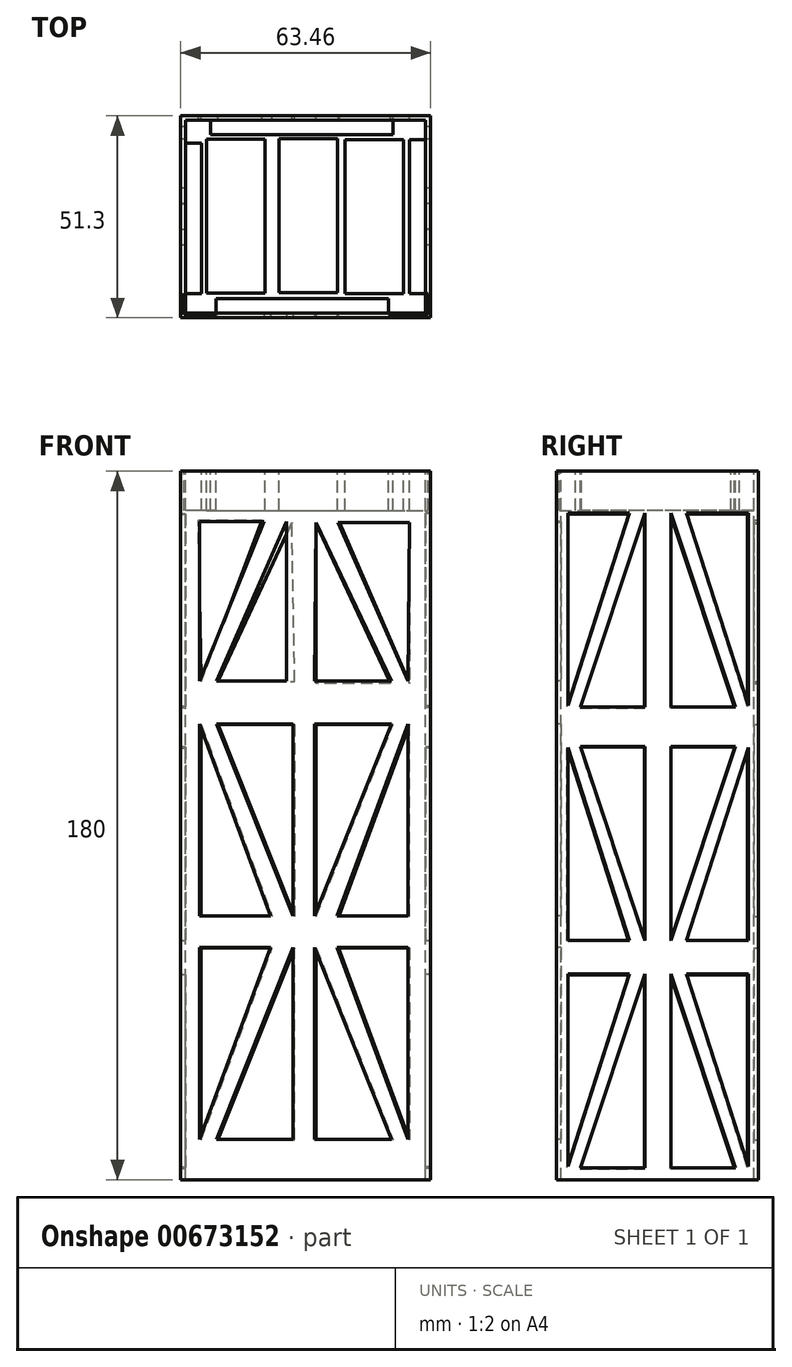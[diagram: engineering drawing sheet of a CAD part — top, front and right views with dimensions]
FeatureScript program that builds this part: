
annotation { "Feature Type Name" : "Feature", "Feature Type Description" : "" }
export const myFeature = defineFeature(function(context is Context, id is Id, definition is map)
    precondition{}
    {
        {
            var Q0;
            Q0=qCreatedBy(makeId("Top.planeOp"),FACE);
            var sketch = newSketch(context, id + "F0", { "sketchPlane" : qUnion([Q0])});
            skLineSegment(sketch, "E0.bottom", {"start": v(-30.5, 24.5) * mm, "end": v(30.5, 24.5) * mm});
            skLineSegment(sketch, "E0.top", {"start": v(-30.5, -24.5) * mm, "end": v(30.5, -24.5) * mm});
            skLineSegment(sketch, "E0.left", {"start": v(-30.5, 24.5) * mm, "end": v(-30.5, -24.5) * mm});
            skLineSegment(sketch, "E0.right", {"start": v(30.5, 24.5) * mm, "end": v(30.5, -24.5) * mm});
            skPoint(sketch, "E0.middle", {"position": v(0, 0) * mm});
            skLineSegment(sketch, "E1.bottom", {"start": v(-31.73, 25.65) * mm, "end": v(31.73, 25.65) * mm});
            skLineSegment(sketch, "E1.top", {"start": v(-31.73, -25.65) * mm, "end": v(31.73, -25.65) * mm});
            skLineSegment(sketch, "E1.left", {"start": v(-31.73, 25.65) * mm, "end": v(-31.73, -25.65) * mm});
            skLineSegment(sketch, "E1.right", {"start": v(31.73, 25.65) * mm, "end": v(31.73, -25.65) * mm});
            skSolve(sketch);
        }
        {
            var Q0;
            Q0=qSketchRegion(id+"F0",true);
            var Q1;
            Q1=qSketchRegion(id+"F2",true);
            extrude(context, id + "F1", {"entities" : qUnion([Q0, Q1]), "oppositeDirection" : true, "depth" : 180 * mm, "offsetDistance" : 25 * mm});
        }
        {
            var Q0;
            Q0=qCreatedBy(makeId("Front.planeOp"),FACE);
            var sketch = newSketch(context, id + "F2", { "sketchPlane" : qUnion([Q0])});
            skLineSegment(sketch, "E2", {"start": v(-37.52, 0) * mm, "end": v(-37.52, -20) * mm});
            skLineSegment(sketch, "E3", {"start": v(38.63, 0) * mm, "end": v(38.63, -20) * mm});
            skSolve(sketch);
        }
        {
            var Q0;
            Q0=qCreatedBy(makeId("Top.planeOp"),FACE);
            var sketch = newSketch(context, id + "F3", { "sketchPlane" : qUnion([Q0])});
            skLineSegment(sketch, "E4.bottom", {"start": v(-26.37, 20.82) * mm, "end": v(26.37, 20.82) * mm});
            skLineSegment(sketch, "E4.top", {"start": v(-26.37, -20.82) * mm, "end": v(26.37, -20.82) * mm});
            skLineSegment(sketch, "E4.left", {"start": v(-26.37, 20.82) * mm, "end": v(-26.37, -20.82) * mm});
            skLineSegment(sketch, "E4.right", {"start": v(26.37, 20.82) * mm, "end": v(26.37, -20.82) * mm});
            skPoint(sketch, "E4.middle", {"position": v(0, 0) * mm});
            skLineSegment(sketch, "E5.bottom", {"start": v(-25.17, 19.7) * mm, "end": v(-10.28, 19.7) * mm});
            skLineSegment(sketch, "E5.top", {"start": v(-25.17, -19.42) * mm, "end": v(-10.28, -19.42) * mm});
            skLineSegment(sketch, "E5.left", {"start": v(-25.17, 19.7) * mm, "end": v(-25.17, -19.42) * mm});
            skLineSegment(sketch, "E5.right", {"start": v(-10.28, 19.7) * mm, "end": v(-10.28, -19.42) * mm});
            skLineSegment(sketch, "E6.bottom", {"start": v(-6.78, 19.79) * mm, "end": v(8.12, 19.79) * mm});
            skLineSegment(sketch, "E6.top", {"start": v(-6.78, -19.34) * mm, "end": v(8.12, -19.34) * mm});
            skLineSegment(sketch, "E6.left", {"start": v(-6.78, 19.79) * mm, "end": v(-6.78, -19.34) * mm});
            skLineSegment(sketch, "E6.right", {"start": v(8.12, 19.79) * mm, "end": v(8.12, -19.34) * mm});
            skLineSegment(sketch, "E7.bottom", {"start": v(10.02, 19.6) * mm, "end": v(24.92, 19.6) * mm});
            skLineSegment(sketch, "E7.top", {"start": v(10.02, -19.52) * mm, "end": v(24.92, -19.52) * mm});
            skLineSegment(sketch, "E7.left", {"start": v(10.02, 19.6) * mm, "end": v(10.02, -19.52) * mm});
            skLineSegment(sketch, "E7.right", {"start": v(24.92, 19.6) * mm, "end": v(24.92, -19.52) * mm});
            skLineSegment(sketch, "E8.bottom", {"start": v(-26.37, 18.7) * mm, "end": v(-30.55, 18.7) * mm});
            skLineSegment(sketch, "E8.top", {"start": v(-26.37, 24.55) * mm, "end": v(-30.55, 24.55) * mm});
            skLineSegment(sketch, "E8.left", {"start": v(-26.37, 18.7) * mm, "end": v(-26.37, 24.55) * mm});
            skLineSegment(sketch, "E8.right", {"start": v(-30.55, 18.7) * mm, "end": v(-30.55, 24.55) * mm});
            skLineSegment(sketch, "E9.bottom", {"start": v(-24.14, 20.82) * mm, "end": v(-26.37, 20.82) * mm});
            skLineSegment(sketch, "E9.top", {"start": v(-24.14, 24.55) * mm, "end": v(-26.37, 24.55) * mm});
            skLineSegment(sketch, "E9.left", {"start": v(-24.14, 20.82) * mm, "end": v(-24.14, 24.55) * mm});
            skLineSegment(sketch, "E9.right", {"start": v(-26.37, 20.82) * mm, "end": v(-26.37, 24.55) * mm});
            skLineSegment(sketch, "E10.bottom", {"start": v(22.27, 24.49) * mm, "end": v(30.52, 24.49) * mm});
            skLineSegment(sketch, "E10.top", {"start": v(22.27, 19.6) * mm, "end": v(30.52, 19.6) * mm});
            skLineSegment(sketch, "E10.left", {"start": v(22.27, 24.49) * mm, "end": v(22.27, 19.6) * mm});
            skLineSegment(sketch, "E10.right", {"start": v(30.52, 24.49) * mm, "end": v(30.52, 19.6) * mm});
            skLineSegment(sketch, "E11.bottom", {"start": v(21.07, -19.52) * mm, "end": v(31.12, -19.52) * mm});
            skLineSegment(sketch, "E11.top", {"start": v(21.07, -24.85) * mm, "end": v(31.12, -24.85) * mm});
            skLineSegment(sketch, "E11.left", {"start": v(21.07, -19.52) * mm, "end": v(21.07, -24.85) * mm});
            skLineSegment(sketch, "E11.right", {"start": v(31.12, -19.52) * mm, "end": v(31.12, -24.85) * mm});
            skLineSegment(sketch, "E12.bottom", {"start": v(-22.78, -24.85) * mm, "end": v(-30.89, -24.85) * mm});
            skLineSegment(sketch, "E12.top", {"start": v(-22.78, -19.52) * mm, "end": v(-30.89, -19.52) * mm});
            skLineSegment(sketch, "E12.left", {"start": v(-22.78, -24.85) * mm, "end": v(-22.78, -19.52) * mm});
            skLineSegment(sketch, "E12.right", {"start": v(-30.89, -24.85) * mm, "end": v(-30.89, -19.52) * mm});
            skSolve(sketch);
        }
        {
            var Q0;
            Q0=qSketchRegion(id+"F3",true);
            extrude(context, id + "F4", {"entities" : qUnion([Q0]), "oppositeDirection" : true, "depth" : 10 * mm, "offsetDistance" : 25 * mm});
        }
        {
            var Q0;
            Q0=sQuery(id+"F0.wireOp",EDGE,"E1.left");
            var Q1;
            Q1=sQuery(id+"F0.wireOp",EDGE,"E0.left");
            var Q2;
            Q2=sQuery(id+"F0.wireOp",EDGE,"E0.bottom");
            var Q3;
            Q3=sQuery(id+"F0.wireOp",EDGE,"E1.bottom");
            var Q4;
            Q4=sQuery(id+"F0.wireOp",EDGE,"E0.right");
            var Q5;
            Q5=sQuery(id+"F0.wireOp",EDGE,"E1.right");
            var Q6;
            Q6=sQuery(id+"F0.wireOp",EDGE,"E1.top");
            var Q7;
            Q7=sQuery(id+"F0.wireOp",EDGE,"E0.top");
            extrude(context, id + "F5", {"bodyType" : ToolBodyType.SURFACE, "surfaceEntities" : qUnion([Q0, Q1, Q2, Q3, Q4, Q5, Q6, Q7]), "depth" : 20 * mm, "offsetDistance" : 25 * mm});
        }
        {
            var Q0;
            Q0=makeQuery(id+"F1.opExtrude","SWEPT_FACE",FACE,{"disambiguationData":[OSD([sQuery(id+"F0.wireOp",EDGE,"E1.top")])]});
            var sketch = newSketch(context, id + "F6", { "sketchPlane" : qUnion([Q0])});
            skLineSegment(sketch, "E13", {"start": v(-26.9, -12.74) * mm, "end": v(-10.52, -12.74) * mm});
            skLineSegment(sketch, "E14", {"start": v(-26.9, -12.74) * mm, "end": v(-26.9, -53.34) * mm});
            skLineSegment(sketch, "E15", {"start": v(-26.9, -53.34) * mm, "end": v(-10.52, -12.74) * mm});
            skLineSegment(sketch, "E16", {"start": v(-22.62, -53.34) * mm, "end": v(-4.82, -53.34) * mm});
            skLineSegment(sketch, "E17", {"start": v(-4.82, -53.34) * mm, "end": v(-4.82, -12.74) * mm});
            skLineSegment(sketch, "E18", {"start": v(-4.82, -12.74) * mm, "end": v(-22.62, -53.34) * mm});
            skLineSegment(sketch, "E19.MirrorCS", {"start": v(26.08, -53.34) * mm, "end": v(8.3, -13.02) * mm});
            skLineSegment(sketch, "E20.MirrorCS", {"start": v(21.8, -53.34) * mm, "end": v(2.32, -53.34) * mm});
            skLineSegment(sketch, "E21.MirrorCS", {"start": v(2.32, -53.34) * mm, "end": v(2.6, -13.02) * mm});
            skLineSegment(sketch, "E22.MirrorCS", {"start": v(2.6, -13.02) * mm, "end": v(21.8, -53.34) * mm});
            skLineSegment(sketch, "E23.MirrorCS", {"start": v(26.36, -13.02) * mm, "end": v(26.08, -53.34) * mm});
            skLineSegment(sketch, "E24.MirrorCS", {"start": v(26.36, -13.02) * mm, "end": v(8.3, -13.02) * mm});
            skLineSegment(sketch, "E25.MirrorCS", {"start": v(21.8, -64.27) * mm, "end": v(2.32, -64.27) * mm});
            skLineSegment(sketch, "E26.MirrorCS", {"start": v(-3.14, -112.97) * mm, "end": v(-22.62, -64.27) * mm});
            skLineSegment(sketch, "E27.MirrorCS", {"start": v(2.32, -64.27) * mm, "end": v(2.32, -112.97) * mm});
            skLineSegment(sketch, "E28.MirrorCS", {"start": v(2.32, -112.97) * mm, "end": v(21.8, -64.27) * mm});
            skLineSegment(sketch, "E29.MirrorCS", {"start": v(-3.14, -64.27) * mm, "end": v(-3.14, -112.97) * mm});
            skLineSegment(sketch, "E30.MirrorCS", {"start": v(26.08, -64.27) * mm, "end": v(8.02, -112.97) * mm});
            skLineSegment(sketch, "E31.MirrorCS", {"start": v(-26.9, -64.27) * mm, "end": v(-8.84, -112.97) * mm});
            skLineSegment(sketch, "E32.MirrorCS", {"start": v(-26.9, -112.97) * mm, "end": v(-26.9, -64.27) * mm});
            skLineSegment(sketch, "E33.MirrorCS", {"start": v(-26.9, -112.97) * mm, "end": v(-8.84, -112.97) * mm});
            skLineSegment(sketch, "E34.MirrorCS", {"start": v(26.08, -112.97) * mm, "end": v(8.02, -112.97) * mm});
            skLineSegment(sketch, "E35.MirrorCS", {"start": v(-22.62, -64.27) * mm, "end": v(-3.14, -64.27) * mm});
            skLineSegment(sketch, "E36.MirrorCS", {"start": v(26.08, -112.97) * mm, "end": v(26.08, -64.27) * mm});
            skLineSegment(sketch, "E37.MirrorCS", {"start": v(26.08, -121.05) * mm, "end": v(26.08, -169.75) * mm});
            skLineSegment(sketch, "E38.MirrorCS", {"start": v(26.08, -169.75) * mm, "end": v(8.02, -121.05) * mm});
            skLineSegment(sketch, "E39.MirrorCS", {"start": v(26.08, -121.05) * mm, "end": v(8.02, -121.05) * mm});
            skLineSegment(sketch, "E40.MirrorCS", {"start": v(2.32, -121.05) * mm, "end": v(21.8, -169.75) * mm});
            skLineSegment(sketch, "E41.MirrorCS", {"start": v(-3.14, -121.05) * mm, "end": v(-22.62, -169.75) * mm});
            skLineSegment(sketch, "E42.MirrorCS", {"start": v(-26.9, -121.05) * mm, "end": v(-26.9, -169.75) * mm});
            skLineSegment(sketch, "E43.MirrorCS", {"start": v(-3.14, -169.75) * mm, "end": v(-3.14, -121.05) * mm});
            skLineSegment(sketch, "E44.MirrorCS", {"start": v(-26.9, -169.75) * mm, "end": v(-8.84, -121.05) * mm});
            skLineSegment(sketch, "E45.MirrorCS", {"start": v(-22.62, -169.75) * mm, "end": v(-3.14, -169.75) * mm});
            skLineSegment(sketch, "E46.MirrorCS", {"start": v(-26.9, -121.05) * mm, "end": v(-8.84, -121.05) * mm});
            skLineSegment(sketch, "E47.MirrorCS", {"start": v(21.8, -169.75) * mm, "end": v(2.32, -169.75) * mm});
            skLineSegment(sketch, "E48.MirrorCS", {"start": v(2.32, -169.75) * mm, "end": v(2.32, -121.05) * mm});
            skSolve(sketch);
        }
        {
            var Q0;
            Q0=makeQuery(id+"F6.imprint","IMPRINT",FACE,{"disambiguationData":[TD([[makeQuery(id+"F6.imprint","IMPRINT",EDGE,{"derivedFrom":sQuery(id+"F6.wireOp",EDGE,"E16")}),1.0]])]});
            var Q1;
            Q1=makeQuery(id+"F6.imprint","IMPRINT",FACE,{"disambiguationData":[TD([[makeQuery(id+"F6.imprint","IMPRINT",EDGE,{"derivedFrom":sQuery(id+"F6.wireOp",EDGE,"E13")}),-1.0]])]});
            var Q2;
            Q2=makeQuery(id+"F6.imprint","IMPRINT",FACE,{"disambiguationData":[TD([[makeQuery(id+"F6.imprint","IMPRINT",EDGE,{"derivedFrom":sQuery(id+"F6.wireOp",EDGE,"E20.MirrorCS")}),-1.0]])]});
            var Q3;
            Q3=makeQuery(id+"F6.imprint","IMPRINT",FACE,{"disambiguationData":[TD([[makeQuery(id+"F6.imprint","IMPRINT",EDGE,{"derivedFrom":sQuery(id+"F6.wireOp",EDGE,"E19.MirrorCS")}),-1.0]])]});
            var Q4;
            Q4=makeQuery(id+"F6.imprint","IMPRINT",FACE,{"disambiguationData":[TD([[makeQuery(id+"F6.imprint","IMPRINT",EDGE,{"derivedFrom":sQuery(id+"F6.wireOp",EDGE,"E31.MirrorCS")}),-1.0]])]});
            var Q5;
            Q5=makeQuery(id+"F6.imprint","IMPRINT",FACE,{"disambiguationData":[TD([[makeQuery(id+"F6.imprint","IMPRINT",EDGE,{"derivedFrom":sQuery(id+"F6.wireOp",EDGE,"E26.MirrorCS")}),-1.0]])]});
            var Q6;
            Q6=makeQuery(id+"F6.imprint","IMPRINT",FACE,{"disambiguationData":[TD([[makeQuery(id+"F6.imprint","IMPRINT",EDGE,{"derivedFrom":sQuery(id+"F6.wireOp",EDGE,"E25.MirrorCS")}),1.0]])]});
            var Q7;
            Q7=makeQuery(id+"F6.imprint","IMPRINT",FACE,{"disambiguationData":[TD([[makeQuery(id+"F6.imprint","IMPRINT",EDGE,{"derivedFrom":sQuery(id+"F6.wireOp",EDGE,"E30.MirrorCS")}),1.0]])]});
            var Q8;
            Q8=makeQuery(id+"F6.imprint","IMPRINT",FACE,{"disambiguationData":[TD([[makeQuery(id+"F6.imprint","IMPRINT",EDGE,{"derivedFrom":sQuery(id+"F6.wireOp",EDGE,"E37.MirrorCS")}),-1.0]])]});
            var Q9;
            Q9=makeQuery(id+"F6.imprint","IMPRINT",FACE,{"disambiguationData":[TD([[makeQuery(id+"F6.imprint","IMPRINT",EDGE,{"derivedFrom":sQuery(id+"F6.wireOp",EDGE,"E40.MirrorCS")}),-1.0]])]});
            var Q10;
            Q10=makeQuery(id+"F6.imprint","IMPRINT",FACE,{"disambiguationData":[TD([[makeQuery(id+"F6.imprint","IMPRINT",EDGE,{"derivedFrom":sQuery(id+"F6.wireOp",EDGE,"E41.MirrorCS")}),1.0]])]});
            var Q11;
            Q11=makeQuery(id+"F6.imprint","IMPRINT",FACE,{"disambiguationData":[TD([[makeQuery(id+"F6.imprint","IMPRINT",EDGE,{"derivedFrom":sQuery(id+"F6.wireOp",EDGE,"E42.MirrorCS")}),1.0]])]});
            extrude(context, id + "F7", {"entities" : qUnion([Q0, Q1, Q2, Q3, Q4, Q5, Q6, Q7, Q8, Q9, Q10, Q11]), "oppositeDirection" : true, "depth" : 5 * mm, "offsetDistance" : 25 * mm});
        }
        {
            var Q0;
            Q0=makeQuery(id+"F7.opExtrude","SWEPT_BODY",BODY,{"disambiguationData":[OSD([sQuery(id+"F6.wireOp",EDGE,"E13"),sQuery(id+"F6.wireOp",EDGE,"E14"),sQuery(id+"F6.wireOp",EDGE,"E15")])]});
            var Q1;
            Q1=makeQuery(id+"F7.opExtrude","SWEPT_BODY",BODY,{"disambiguationData":[OSD([sQuery(id+"F6.wireOp",EDGE,"E16"),sQuery(id+"F6.wireOp",EDGE,"E17"),sQuery(id+"F6.wireOp",EDGE,"E18")])]});
            var Q2;
            Q2=makeQuery(id+"F7.opExtrude","SWEPT_BODY",BODY,{"disambiguationData":[OSD([sQuery(id+"F6.wireOp",EDGE,"E20.MirrorCS"),sQuery(id+"F6.wireOp",EDGE,"E21.MirrorCS"),sQuery(id+"F6.wireOp",EDGE,"E22.MirrorCS")])]});
            var Q3;
            Q3=makeQuery(id+"F7.opExtrude","SWEPT_BODY",BODY,{"disambiguationData":[OSD([sQuery(id+"F6.wireOp",EDGE,"E19.MirrorCS"),sQuery(id+"F6.wireOp",EDGE,"E23.MirrorCS"),sQuery(id+"F6.wireOp",EDGE,"E24.MirrorCS")])]});
            var Q4;
            Q4=makeQuery(id+"F7.opExtrude","SWEPT_BODY",BODY,{"disambiguationData":[OSD([sQuery(id+"F6.wireOp",EDGE,"E30.MirrorCS"),sQuery(id+"F6.wireOp",EDGE,"E34.MirrorCS"),sQuery(id+"F6.wireOp",EDGE,"E36.MirrorCS")])]});
            var Q5;
            Q5=makeQuery(id+"F7.opExtrude","SWEPT_BODY",BODY,{"disambiguationData":[OSD([sQuery(id+"F6.wireOp",EDGE,"E25.MirrorCS"),sQuery(id+"F6.wireOp",EDGE,"E27.MirrorCS"),sQuery(id+"F6.wireOp",EDGE,"E28.MirrorCS")])]});
            var Q6;
            Q6=makeQuery(id+"F7.opExtrude","SWEPT_BODY",BODY,{"disambiguationData":[OSD([sQuery(id+"F6.wireOp",EDGE,"E26.MirrorCS"),sQuery(id+"F6.wireOp",EDGE,"E29.MirrorCS"),sQuery(id+"F6.wireOp",EDGE,"E35.MirrorCS")])]});
            var Q7;
            Q7=makeQuery(id+"F7.opExtrude","SWEPT_BODY",BODY,{"disambiguationData":[OSD([sQuery(id+"F6.wireOp",EDGE,"E31.MirrorCS"),sQuery(id+"F6.wireOp",EDGE,"E32.MirrorCS"),sQuery(id+"F6.wireOp",EDGE,"E33.MirrorCS")])]});
            var Q8;
            Q8=makeQuery(id+"F7.opExtrude","SWEPT_BODY",BODY,{"disambiguationData":[OSD([sQuery(id+"F6.wireOp",EDGE,"E42.MirrorCS"),sQuery(id+"F6.wireOp",EDGE,"E44.MirrorCS"),sQuery(id+"F6.wireOp",EDGE,"E46.MirrorCS")])]});
            var Q9;
            Q9=makeQuery(id+"F7.opExtrude","SWEPT_BODY",BODY,{"disambiguationData":[OSD([sQuery(id+"F6.wireOp",EDGE,"E41.MirrorCS"),sQuery(id+"F6.wireOp",EDGE,"E43.MirrorCS"),sQuery(id+"F6.wireOp",EDGE,"E45.MirrorCS")])]});
            var Q10;
            Q10=makeQuery(id+"F7.opExtrude","SWEPT_BODY",BODY,{"disambiguationData":[OSD([sQuery(id+"F6.wireOp",EDGE,"E40.MirrorCS"),sQuery(id+"F6.wireOp",EDGE,"E47.MirrorCS"),sQuery(id+"F6.wireOp",EDGE,"E48.MirrorCS")])]});
            var Q11;
            Q11=makeQuery(id+"F7.opExtrude","SWEPT_BODY",BODY,{"disambiguationData":[OSD([sQuery(id+"F6.wireOp",EDGE,"E37.MirrorCS"),sQuery(id+"F6.wireOp",EDGE,"E38.MirrorCS"),sQuery(id+"F6.wireOp",EDGE,"E39.MirrorCS")])]});
            var Q12;
            Q12=makeQuery(id+"F1.opExtrude","SWEPT_BODY",BODY,{"disambiguationData":[OSD([sQuery(id+"F0.wireOp",EDGE,"E0.bottom"),sQuery(id+"F0.wireOp",EDGE,"E0.top"),sQuery(id+"F0.wireOp",EDGE,"E0.left"),sQuery(id+"F0.wireOp",EDGE,"E0.right"),sQuery(id+"F0.wireOp",EDGE,"E1.bottom"),sQuery(id+"F0.wireOp",EDGE,"E1.top"),sQuery(id+"F0.wireOp",EDGE,"E1.left"),sQuery(id+"F0.wireOp",EDGE,"E1.right")])]});
            booleanBodies(context, id + "F8", {"operationType" : BooleanOperationType.SUBTRACTION, "tools" : qUnion([Q0, Q1, Q2, Q3, Q4, Q5, Q6, Q7, Q8, Q9, Q10, Q11]), "targets" : qUnion([Q12])});
        }
        {
            var Q0;
            Q0=makeQuery(id+"F1.opExtrude","SWEPT_FACE",FACE,{"disambiguationData":[OSD([sQuery(id+"F0.wireOp",EDGE,"E1.left")])]});
            var sketch = newSketch(context, id + "F9", { "sketchPlane" : qUnion([Q0])});
            skLineSegment(sketch, "E49", {"start": v(-22.91, -10.86) * mm, "end": v(-22.91, -59.77) * mm});
            skLineSegment(sketch, "E50", {"start": v(-22.91, -59.77) * mm, "end": v(-7.26, -10.86) * mm});
            skLineSegment(sketch, "E51", {"start": v(-7.26, -10.86) * mm, "end": v(-22.91, -10.86) * mm});
            skLineSegment(sketch, "E52", {"start": v(-3.33, -10.86) * mm, "end": v(-19.7, -60.13) * mm});
            skLineSegment(sketch, "E53", {"start": v(-19.7, -60.13) * mm, "end": v(-3.33, -60.13) * mm});
            skLineSegment(sketch, "E54", {"start": v(-3.33, -60.13) * mm, "end": v(-3.33, -10.86) * mm});
            skLineSegment(sketch, "E55.MirrorCS", {"start": v(22.91, -59.77) * mm, "end": v(7.25, -10.83) * mm});
            skLineSegment(sketch, "E56.MirrorCS", {"start": v(7.25, -10.83) * mm, "end": v(22.91, -10.83) * mm});
            skLineSegment(sketch, "E57.MirrorCS", {"start": v(3.33, -10.83) * mm, "end": v(19.7, -60.13) * mm});
            skLineSegment(sketch, "E58.MirrorCS", {"start": v(3.33, -60.13) * mm, "end": v(3.33, -10.83) * mm});
            skLineSegment(sketch, "E59.MirrorCS", {"start": v(19.7, -60.13) * mm, "end": v(3.33, -60.13) * mm});
            skLineSegment(sketch, "E60.MirrorCS", {"start": v(22.91, -10.83) * mm, "end": v(22.91, -59.77) * mm});
            skLineSegment(sketch, "E61.MirrorCS", {"start": v(-22.91, -119.4) * mm, "end": v(-22.91, -70.45) * mm});
            skLineSegment(sketch, "E62.MirrorCS", {"start": v(-19.7, -70.1) * mm, "end": v(-3.33, -70.1) * mm});
            skLineSegment(sketch, "E63.MirrorCS", {"start": v(-22.91, -70.45) * mm, "end": v(-7.25, -119.4) * mm});
            skLineSegment(sketch, "E64.MirrorCS", {"start": v(-3.33, -119.4) * mm, "end": v(-19.7, -70.1) * mm});
            skLineSegment(sketch, "E65.MirrorCS", {"start": v(-7.25, -119.4) * mm, "end": v(-22.91, -119.4) * mm});
            skLineSegment(sketch, "E66.MirrorCS", {"start": v(-3.33, -70.1) * mm, "end": v(-3.33, -119.4) * mm});
            skLineSegment(sketch, "E67.MirrorCS", {"start": v(3.33, -119.4) * mm, "end": v(19.7, -70.1) * mm});
            skLineSegment(sketch, "E68.MirrorCS", {"start": v(22.91, -119.4) * mm, "end": v(22.91, -70.45) * mm});
            skLineSegment(sketch, "E69.MirrorCS", {"start": v(7.25, -119.4) * mm, "end": v(22.91, -119.4) * mm});
            skLineSegment(sketch, "E70.MirrorCS", {"start": v(3.33, -70.1) * mm, "end": v(3.33, -119.4) * mm});
            skLineSegment(sketch, "E71.MirrorCS", {"start": v(22.91, -70.45) * mm, "end": v(7.25, -119.4) * mm});
            skLineSegment(sketch, "E72.MirrorCS", {"start": v(19.7, -70.1) * mm, "end": v(3.33, -70.1) * mm});
            skLineSegment(sketch, "E73.MirrorCS", {"start": v(22.91, -127.94) * mm, "end": v(22.91, -176.88) * mm});
            skLineSegment(sketch, "E74.MirrorCS", {"start": v(3.33, -177.24) * mm, "end": v(3.33, -127.94) * mm});
            skLineSegment(sketch, "E75.MirrorCS", {"start": v(3.33, -127.94) * mm, "end": v(19.7, -177.24) * mm});
            skLineSegment(sketch, "E76.MirrorCS", {"start": v(-22.91, -127.94) * mm, "end": v(-22.91, -176.88) * mm});
            skLineSegment(sketch, "E77.MirrorCS", {"start": v(-7.25, -127.94) * mm, "end": v(-22.91, -127.94) * mm});
            skLineSegment(sketch, "E78.MirrorCS", {"start": v(22.91, -176.88) * mm, "end": v(7.25, -127.94) * mm});
            skLineSegment(sketch, "E79.MirrorCS", {"start": v(-19.7, -177.24) * mm, "end": v(-3.33, -177.24) * mm});
            skLineSegment(sketch, "E80.MirrorCS", {"start": v(-3.33, -177.24) * mm, "end": v(-3.33, -127.94) * mm});
            skLineSegment(sketch, "E81.MirrorCS", {"start": v(-22.91, -176.88) * mm, "end": v(-7.25, -127.94) * mm});
            skLineSegment(sketch, "E82.MirrorCS", {"start": v(19.7, -177.24) * mm, "end": v(3.33, -177.24) * mm});
            skLineSegment(sketch, "E83.MirrorCS", {"start": v(-3.33, -127.94) * mm, "end": v(-19.7, -177.24) * mm});
            skLineSegment(sketch, "E84.MirrorCS", {"start": v(7.25, -127.94) * mm, "end": v(22.91, -127.94) * mm});
            skSolve(sketch);
        }
        {
            var Q0;
            Q0=makeQuery(id+"F9.imprint","IMPRINT",FACE,{"disambiguationData":[TD([[makeQuery(id+"F9.imprint","IMPRINT",EDGE,{"derivedFrom":sQuery(id+"F9.wireOp",EDGE,"E52")}),1.0]])]});
            var Q1;
            Q1=makeQuery(id+"F9.imprint","IMPRINT",FACE,{"disambiguationData":[TD([[makeQuery(id+"F9.imprint","IMPRINT",EDGE,{"derivedFrom":sQuery(id+"F9.wireOp",EDGE,"E57.MirrorCS")}),-1.0]])]});
            var Q2;
            Q2=makeQuery(id+"F9.imprint","IMPRINT",FACE,{"disambiguationData":[TD([[makeQuery(id+"F9.imprint","IMPRINT",EDGE,{"derivedFrom":sQuery(id+"F9.wireOp",EDGE,"E55.MirrorCS")}),-1.0]])]});
            var Q3;
            Q3=makeQuery(id+"F9.imprint","IMPRINT",FACE,{"disambiguationData":[TD([[makeQuery(id+"F9.imprint","IMPRINT",EDGE,{"derivedFrom":sQuery(id+"F9.wireOp",EDGE,"E62.MirrorCS")}),-1.0]])]});
            var Q4;
            Q4=makeQuery(id+"F9.imprint","IMPRINT",FACE,{"disambiguationData":[TD([[makeQuery(id+"F9.imprint","IMPRINT",EDGE,{"derivedFrom":sQuery(id+"F9.wireOp",EDGE,"E61.MirrorCS")}),-1.0]])]});
            var Q5;
            Q5=makeQuery(id+"F9.imprint","IMPRINT",FACE,{"disambiguationData":[TD([[makeQuery(id+"F9.imprint","IMPRINT",EDGE,{"derivedFrom":sQuery(id+"F9.wireOp",EDGE,"E68.MirrorCS")}),1.0]])]});
            var Q6;
            Q6=makeQuery(id+"F9.imprint","IMPRINT",FACE,{"disambiguationData":[TD([[makeQuery(id+"F9.imprint","IMPRINT",EDGE,{"derivedFrom":sQuery(id+"F9.wireOp",EDGE,"E76.MirrorCS")}),1.0]])]});
            var Q7;
            Q7=makeQuery(id+"F9.imprint","IMPRINT",FACE,{"disambiguationData":[TD([[makeQuery(id+"F9.imprint","IMPRINT",EDGE,{"derivedFrom":sQuery(id+"F9.wireOp",EDGE,"E79.MirrorCS")}),1.0]])]});
            var Q8;
            Q8=makeQuery(id+"F9.imprint","IMPRINT",FACE,{"disambiguationData":[TD([[makeQuery(id+"F9.imprint","IMPRINT",EDGE,{"derivedFrom":sQuery(id+"F9.wireOp",EDGE,"E74.MirrorCS")}),-1.0]])]});
            var Q9;
            Q9=makeQuery(id+"F9.imprint","IMPRINT",FACE,{"disambiguationData":[TD([[makeQuery(id+"F9.imprint","IMPRINT",EDGE,{"derivedFrom":sQuery(id+"F9.wireOp",EDGE,"E73.MirrorCS")}),-1.0]])]});
            var Q10;
            Q10=makeQuery(id+"F9.imprint","IMPRINT",FACE,{"disambiguationData":[TD([[makeQuery(id+"F9.imprint","IMPRINT",EDGE,{"derivedFrom":sQuery(id+"F9.wireOp",EDGE,"E67.MirrorCS")}),1.0]])]});
            var Q11;
            Q11=makeQuery(id+"F9.imprint","IMPRINT",FACE,{"disambiguationData":[TD([[makeQuery(id+"F9.imprint","IMPRINT",EDGE,{"derivedFrom":sQuery(id+"F9.wireOp",EDGE,"E49")}),1.0]])]});
            extrude(context, id + "F10", {"entities" : qUnion([Q0, Q1, Q2, Q3, Q4, Q5, Q6, Q7, Q8, Q9, Q10, Q11]), "oppositeDirection" : true, "depth" : 5 * mm, "offsetDistance" : 25 * mm});
        }
        {
            var Q0;
            Q0=makeQuery(id+"F10.opExtrude","SWEPT_BODY",BODY,{"disambiguationData":[OSD([sQuery(id+"F9.wireOp",EDGE,"E52"),sQuery(id+"F9.wireOp",EDGE,"E53"),sQuery(id+"F9.wireOp",EDGE,"E54")])]});
            var Q1;
            Q1=makeQuery(id+"F10.opExtrude","SWEPT_BODY",BODY,{"disambiguationData":[OSD([sQuery(id+"F9.wireOp",EDGE,"E57.MirrorCS"),sQuery(id+"F9.wireOp",EDGE,"E58.MirrorCS"),sQuery(id+"F9.wireOp",EDGE,"E59.MirrorCS")])]});
            var Q2;
            Q2=makeQuery(id+"F10.opExtrude","SWEPT_BODY",BODY,{"disambiguationData":[OSD([sQuery(id+"F9.wireOp",EDGE,"E55.MirrorCS"),sQuery(id+"F9.wireOp",EDGE,"E56.MirrorCS"),sQuery(id+"F9.wireOp",EDGE,"E60.MirrorCS")])]});
            var Q3;
            Q3=makeQuery(id+"F10.opExtrude","SWEPT_BODY",BODY,{"disambiguationData":[OSD([sQuery(id+"F9.wireOp",EDGE,"E49"),sQuery(id+"F9.wireOp",EDGE,"E50"),sQuery(id+"F9.wireOp",EDGE,"E51")])]});
            var Q4;
            Q4=makeQuery(id+"F10.opExtrude","SWEPT_BODY",BODY,{"disambiguationData":[OSD([sQuery(id+"F9.wireOp",EDGE,"E61.MirrorCS"),sQuery(id+"F9.wireOp",EDGE,"E63.MirrorCS"),sQuery(id+"F9.wireOp",EDGE,"E65.MirrorCS")])]});
            var Q5;
            Q5=makeQuery(id+"F10.opExtrude","SWEPT_BODY",BODY,{"disambiguationData":[OSD([sQuery(id+"F9.wireOp",EDGE,"E62.MirrorCS"),sQuery(id+"F9.wireOp",EDGE,"E64.MirrorCS"),sQuery(id+"F9.wireOp",EDGE,"E66.MirrorCS")])]});
            var Q6;
            Q6=makeQuery(id+"F10.opExtrude","SWEPT_BODY",BODY,{"disambiguationData":[OSD([sQuery(id+"F9.wireOp",EDGE,"E67.MirrorCS"),sQuery(id+"F9.wireOp",EDGE,"E70.MirrorCS"),sQuery(id+"F9.wireOp",EDGE,"E72.MirrorCS")])]});
            var Q7;
            Q7=makeQuery(id+"F10.opExtrude","SWEPT_BODY",BODY,{"disambiguationData":[OSD([sQuery(id+"F9.wireOp",EDGE,"E68.MirrorCS"),sQuery(id+"F9.wireOp",EDGE,"E69.MirrorCS"),sQuery(id+"F9.wireOp",EDGE,"E71.MirrorCS")])]});
            var Q8;
            Q8=makeQuery(id+"F10.opExtrude","SWEPT_BODY",BODY,{"disambiguationData":[OSD([sQuery(id+"F9.wireOp",EDGE,"E73.MirrorCS"),sQuery(id+"F9.wireOp",EDGE,"E78.MirrorCS"),sQuery(id+"F9.wireOp",EDGE,"E84.MirrorCS")])]});
            var Q9;
            Q9=makeQuery(id+"F10.opExtrude","SWEPT_BODY",BODY,{"disambiguationData":[OSD([sQuery(id+"F9.wireOp",EDGE,"E74.MirrorCS"),sQuery(id+"F9.wireOp",EDGE,"E75.MirrorCS"),sQuery(id+"F9.wireOp",EDGE,"E82.MirrorCS")])]});
            var Q10;
            Q10=makeQuery(id+"F10.opExtrude","SWEPT_BODY",BODY,{"disambiguationData":[OSD([sQuery(id+"F9.wireOp",EDGE,"E79.MirrorCS"),sQuery(id+"F9.wireOp",EDGE,"E80.MirrorCS"),sQuery(id+"F9.wireOp",EDGE,"E83.MirrorCS")])]});
            var Q11;
            Q11=makeQuery(id+"F10.opExtrude","SWEPT_BODY",BODY,{"disambiguationData":[OSD([sQuery(id+"F9.wireOp",EDGE,"E76.MirrorCS"),sQuery(id+"F9.wireOp",EDGE,"E77.MirrorCS"),sQuery(id+"F9.wireOp",EDGE,"E81.MirrorCS")])]});
            var Q12;
            Q12=makeQuery(id+"F1.opExtrude","SWEPT_BODY",BODY,{"disambiguationData":[OSD([sQuery(id+"F0.wireOp",EDGE,"E0.bottom"),sQuery(id+"F0.wireOp",EDGE,"E0.top"),sQuery(id+"F0.wireOp",EDGE,"E0.left"),sQuery(id+"F0.wireOp",EDGE,"E0.right"),sQuery(id+"F0.wireOp",EDGE,"E1.bottom"),sQuery(id+"F0.wireOp",EDGE,"E1.top"),sQuery(id+"F0.wireOp",EDGE,"E1.left"),sQuery(id+"F0.wireOp",EDGE,"E1.right")])]});
            booleanBodies(context, id + "F11", {"operationType" : BooleanOperationType.SUBTRACTION, "tools" : qUnion([Q0, Q1, Q2, Q3, Q4, Q5, Q6, Q7, Q8, Q9, Q10, Q11]), "targets" : qUnion([Q12])});
        }
        {
            var Q0;
            Q0=makeQuery(id+"F1.opExtrude","SWEPT_FACE",FACE,{"disambiguationData":[OSD([sQuery(id+"F0.wireOp",EDGE,"E1.right")])]});
            var sketch = newSketch(context, id + "F12", { "sketchPlane" : qUnion([Q0])});
            skLineSegment(sketch, "E85", {"start": v(-22.75, -10.65) * mm, "end": v(-22.75, -59.56) * mm});
            skLineSegment(sketch, "E86", {"start": v(-22.75, -59.56) * mm, "end": v(-7.1, -10.65) * mm});
            skLineSegment(sketch, "E87", {"start": v(-7.1, -10.65) * mm, "end": v(-22.75, -10.65) * mm});
            skLineSegment(sketch, "E88", {"start": v(-3.17, -10.65) * mm, "end": v(-19.54, -59.92) * mm});
            skLineSegment(sketch, "E89", {"start": v(-19.54, -59.92) * mm, "end": v(-3.17, -59.92) * mm});
            skLineSegment(sketch, "E90", {"start": v(-3.17, -59.92) * mm, "end": v(-3.17, -10.65) * mm});
            skLineSegment(sketch, "E91.MirrorCS", {"start": v(23.08, -59.56) * mm, "end": v(7.42, -10.62) * mm});
            skLineSegment(sketch, "E92.MirrorCS", {"start": v(7.42, -10.62) * mm, "end": v(23.08, -10.62) * mm});
            skLineSegment(sketch, "E93.MirrorCS", {"start": v(3.5, -10.62) * mm, "end": v(19.87, -59.92) * mm});
            skLineSegment(sketch, "E94.MirrorCS", {"start": v(3.5, -59.92) * mm, "end": v(3.5, -10.62) * mm});
            skLineSegment(sketch, "E95.MirrorCS", {"start": v(19.87, -59.92) * mm, "end": v(3.5, -59.92) * mm});
            skLineSegment(sketch, "E96.MirrorCS", {"start": v(23.08, -10.62) * mm, "end": v(23.08, -59.56) * mm});
            skLineSegment(sketch, "E97.MirrorCS", {"start": v(-22.75, -119.19) * mm, "end": v(-22.75, -70.24) * mm});
            skLineSegment(sketch, "E98.MirrorCS", {"start": v(-19.54, -69.88) * mm, "end": v(-3.17, -69.88) * mm});
            skLineSegment(sketch, "E99.MirrorCS", {"start": v(-22.75, -70.24) * mm, "end": v(-7.09, -119.19) * mm});
            skLineSegment(sketch, "E100.MirrorCS", {"start": v(-3.17, -119.19) * mm, "end": v(-19.54, -69.88) * mm});
            skLineSegment(sketch, "E101.MirrorCS", {"start": v(-7.09, -119.19) * mm, "end": v(-22.75, -119.19) * mm});
            skLineSegment(sketch, "E102.MirrorCS", {"start": v(-3.17, -69.88) * mm, "end": v(-3.17, -119.19) * mm});
            skLineSegment(sketch, "E103.MirrorCS", {"start": v(3.5, -119.19) * mm, "end": v(19.87, -69.88) * mm});
            skLineSegment(sketch, "E104.MirrorCS", {"start": v(23.08, -119.19) * mm, "end": v(23.08, -70.24) * mm});
            skLineSegment(sketch, "E105.MirrorCS", {"start": v(7.42, -119.19) * mm, "end": v(23.08, -119.19) * mm});
            skLineSegment(sketch, "E106.MirrorCS", {"start": v(3.5, -69.88) * mm, "end": v(3.5, -119.19) * mm});
            skLineSegment(sketch, "E107.MirrorCS", {"start": v(23.08, -70.24) * mm, "end": v(7.42, -119.19) * mm});
            skLineSegment(sketch, "E108.MirrorCS", {"start": v(19.87, -69.88) * mm, "end": v(3.5, -69.88) * mm});
            skLineSegment(sketch, "E109.MirrorCS", {"start": v(23.08, -127.73) * mm, "end": v(23.08, -176.67) * mm});
            skLineSegment(sketch, "E110.MirrorCS", {"start": v(3.5, -177.03) * mm, "end": v(3.5, -127.73) * mm});
            skLineSegment(sketch, "E111.MirrorCS", {"start": v(3.5, -127.73) * mm, "end": v(19.87, -177.03) * mm});
            skLineSegment(sketch, "E112.MirrorCS", {"start": v(-22.75, -127.73) * mm, "end": v(-22.75, -176.67) * mm});
            skLineSegment(sketch, "E113.MirrorCS", {"start": v(-7.09, -127.73) * mm, "end": v(-22.75, -127.73) * mm});
            skLineSegment(sketch, "E114.MirrorCS", {"start": v(23.08, -176.67) * mm, "end": v(7.42, -127.73) * mm});
            skLineSegment(sketch, "E115.MirrorCS", {"start": v(-19.54, -177.03) * mm, "end": v(-3.17, -177.03) * mm});
            skLineSegment(sketch, "E116.MirrorCS", {"start": v(-3.17, -177.03) * mm, "end": v(-3.17, -127.73) * mm});
            skLineSegment(sketch, "E117.MirrorCS", {"start": v(-22.75, -176.67) * mm, "end": v(-7.09, -127.73) * mm});
            skLineSegment(sketch, "E118.MirrorCS", {"start": v(19.87, -177.03) * mm, "end": v(3.5, -177.03) * mm});
            skLineSegment(sketch, "E119.MirrorCS", {"start": v(-3.17, -127.73) * mm, "end": v(-19.54, -177.03) * mm});
            skLineSegment(sketch, "E120.MirrorCS", {"start": v(7.42, -127.73) * mm, "end": v(23.08, -127.73) * mm});
            skSolve(sketch);
        }
        {
            var Q0;
            Q0=makeQuery(id+"F12.imprint","IMPRINT",FACE,{"disambiguationData":[TD([[makeQuery(id+"F12.imprint","IMPRINT",EDGE,{"derivedFrom":sQuery(id+"F12.wireOp",EDGE,"E85")}),1.0]])]});
            var Q1;
            Q1=makeQuery(id+"F12.imprint","IMPRINT",FACE,{"disambiguationData":[TD([[makeQuery(id+"F12.imprint","IMPRINT",EDGE,{"derivedFrom":sQuery(id+"F12.wireOp",EDGE,"E88")}),1.0]])]});
            var Q2;
            Q2=makeQuery(id+"F12.imprint","IMPRINT",FACE,{"disambiguationData":[TD([[makeQuery(id+"F12.imprint","IMPRINT",EDGE,{"derivedFrom":sQuery(id+"F12.wireOp",EDGE,"E93.MirrorCS")}),-1.0]])]});
            var Q3;
            Q3=makeQuery(id+"F12.imprint","IMPRINT",FACE,{"disambiguationData":[TD([[makeQuery(id+"F12.imprint","IMPRINT",EDGE,{"derivedFrom":sQuery(id+"F12.wireOp",EDGE,"E91.MirrorCS")}),-1.0]])]});
            var Q4;
            Q4=makeQuery(id+"F12.imprint","IMPRINT",FACE,{"disambiguationData":[TD([[makeQuery(id+"F12.imprint","IMPRINT",EDGE,{"derivedFrom":sQuery(id+"F12.wireOp",EDGE,"E97.MirrorCS")}),-1.0]])]});
            var Q5;
            Q5=makeQuery(id+"F12.imprint","IMPRINT",FACE,{"disambiguationData":[TD([[makeQuery(id+"F12.imprint","IMPRINT",EDGE,{"derivedFrom":sQuery(id+"F12.wireOp",EDGE,"E98.MirrorCS")}),-1.0]])]});
            var Q6;
            Q6=makeQuery(id+"F12.imprint","IMPRINT",FACE,{"disambiguationData":[TD([[makeQuery(id+"F12.imprint","IMPRINT",EDGE,{"derivedFrom":sQuery(id+"F12.wireOp",EDGE,"E103.MirrorCS")}),1.0]])]});
            var Q7;
            Q7=makeQuery(id+"F12.imprint","IMPRINT",FACE,{"disambiguationData":[TD([[makeQuery(id+"F12.imprint","IMPRINT",EDGE,{"derivedFrom":sQuery(id+"F12.wireOp",EDGE,"E104.MirrorCS")}),1.0]])]});
            var Q8;
            Q8=makeQuery(id+"F12.imprint","IMPRINT",FACE,{"disambiguationData":[TD([[makeQuery(id+"F12.imprint","IMPRINT",EDGE,{"derivedFrom":sQuery(id+"F12.wireOp",EDGE,"E109.MirrorCS")}),-1.0]])]});
            var Q9;
            Q9=makeQuery(id+"F12.imprint","IMPRINT",FACE,{"disambiguationData":[TD([[makeQuery(id+"F12.imprint","IMPRINT",EDGE,{"derivedFrom":sQuery(id+"F12.wireOp",EDGE,"E110.MirrorCS")}),-1.0]])]});
            var Q10;
            Q10=makeQuery(id+"F12.imprint","IMPRINT",FACE,{"disambiguationData":[TD([[makeQuery(id+"F12.imprint","IMPRINT",EDGE,{"derivedFrom":sQuery(id+"F12.wireOp",EDGE,"E115.MirrorCS")}),1.0]])]});
            var Q11;
            Q11=makeQuery(id+"F12.imprint","IMPRINT",FACE,{"disambiguationData":[TD([[makeQuery(id+"F12.imprint","IMPRINT",EDGE,{"derivedFrom":sQuery(id+"F12.wireOp",EDGE,"E112.MirrorCS")}),1.0]])]});
            extrude(context, id + "F13", {"entities" : qUnion([Q0, Q1, Q2, Q3, Q4, Q5, Q6, Q7, Q8, Q9, Q10, Q11]), "oppositeDirection" : true, "depth" : 5 * mm, "offsetDistance" : 25 * mm});
        }
        {
            var Q0;
            Q0=makeQuery(id+"F13.opExtrude","SWEPT_BODY",BODY,{"disambiguationData":[OSD([sQuery(id+"F12.wireOp",EDGE,"E85"),sQuery(id+"F12.wireOp",EDGE,"E86"),sQuery(id+"F12.wireOp",EDGE,"E87")])]});
            var Q1;
            Q1=makeQuery(id+"F13.opExtrude","SWEPT_BODY",BODY,{"disambiguationData":[OSD([sQuery(id+"F12.wireOp",EDGE,"E88"),sQuery(id+"F12.wireOp",EDGE,"E89"),sQuery(id+"F12.wireOp",EDGE,"E90")])]});
            var Q2;
            Q2=makeQuery(id+"F13.opExtrude","SWEPT_BODY",BODY,{"disambiguationData":[OSD([sQuery(id+"F12.wireOp",EDGE,"E93.MirrorCS"),sQuery(id+"F12.wireOp",EDGE,"E94.MirrorCS"),sQuery(id+"F12.wireOp",EDGE,"E95.MirrorCS")])]});
            var Q3;
            Q3=makeQuery(id+"F13.opExtrude","SWEPT_BODY",BODY,{"disambiguationData":[OSD([sQuery(id+"F12.wireOp",EDGE,"E91.MirrorCS"),sQuery(id+"F12.wireOp",EDGE,"E92.MirrorCS"),sQuery(id+"F12.wireOp",EDGE,"E96.MirrorCS")])]});
            var Q4;
            Q4=makeQuery(id+"F13.opExtrude","SWEPT_BODY",BODY,{"disambiguationData":[OSD([sQuery(id+"F12.wireOp",EDGE,"E97.MirrorCS"),sQuery(id+"F12.wireOp",EDGE,"E99.MirrorCS"),sQuery(id+"F12.wireOp",EDGE,"E101.MirrorCS")])]});
            var Q5;
            Q5=makeQuery(id+"F13.opExtrude","SWEPT_BODY",BODY,{"disambiguationData":[OSD([sQuery(id+"F12.wireOp",EDGE,"E98.MirrorCS"),sQuery(id+"F12.wireOp",EDGE,"E100.MirrorCS"),sQuery(id+"F12.wireOp",EDGE,"E102.MirrorCS")])]});
            var Q6;
            Q6=makeQuery(id+"F13.opExtrude","SWEPT_BODY",BODY,{"disambiguationData":[OSD([sQuery(id+"F12.wireOp",EDGE,"E103.MirrorCS"),sQuery(id+"F12.wireOp",EDGE,"E106.MirrorCS"),sQuery(id+"F12.wireOp",EDGE,"E108.MirrorCS")])]});
            var Q7;
            Q7=makeQuery(id+"F13.opExtrude","SWEPT_BODY",BODY,{"disambiguationData":[OSD([sQuery(id+"F12.wireOp",EDGE,"E104.MirrorCS"),sQuery(id+"F12.wireOp",EDGE,"E105.MirrorCS"),sQuery(id+"F12.wireOp",EDGE,"E107.MirrorCS")])]});
            var Q8;
            Q8=makeQuery(id+"F13.opExtrude","SWEPT_BODY",BODY,{"disambiguationData":[OSD([sQuery(id+"F12.wireOp",EDGE,"E109.MirrorCS"),sQuery(id+"F12.wireOp",EDGE,"E114.MirrorCS"),sQuery(id+"F12.wireOp",EDGE,"E120.MirrorCS")])]});
            var Q9;
            Q9=makeQuery(id+"F13.opExtrude","SWEPT_BODY",BODY,{"disambiguationData":[OSD([sQuery(id+"F12.wireOp",EDGE,"E110.MirrorCS"),sQuery(id+"F12.wireOp",EDGE,"E111.MirrorCS"),sQuery(id+"F12.wireOp",EDGE,"E118.MirrorCS")])]});
            var Q10;
            Q10=makeQuery(id+"F13.opExtrude","SWEPT_BODY",BODY,{"disambiguationData":[OSD([sQuery(id+"F12.wireOp",EDGE,"E115.MirrorCS"),sQuery(id+"F12.wireOp",EDGE,"E116.MirrorCS"),sQuery(id+"F12.wireOp",EDGE,"E119.MirrorCS")])]});
            var Q11;
            Q11=makeQuery(id+"F13.opExtrude","SWEPT_BODY",BODY,{"disambiguationData":[OSD([sQuery(id+"F12.wireOp",EDGE,"E112.MirrorCS"),sQuery(id+"F12.wireOp",EDGE,"E113.MirrorCS"),sQuery(id+"F12.wireOp",EDGE,"E117.MirrorCS")])]});
            var Q12;
            Q12=makeQuery(id+"F1.opExtrude","SWEPT_BODY",BODY,{"disambiguationData":[OSD([sQuery(id+"F0.wireOp",EDGE,"E0.bottom"),sQuery(id+"F0.wireOp",EDGE,"E0.top"),sQuery(id+"F0.wireOp",EDGE,"E0.left"),sQuery(id+"F0.wireOp",EDGE,"E0.right"),sQuery(id+"F0.wireOp",EDGE,"E1.bottom"),sQuery(id+"F0.wireOp",EDGE,"E1.top"),sQuery(id+"F0.wireOp",EDGE,"E1.left"),sQuery(id+"F0.wireOp",EDGE,"E1.right")])]});
            booleanBodies(context, id + "F14", {"operationType" : BooleanOperationType.SUBTRACTION, "tools" : qUnion([Q0, Q1, Q2, Q3, Q4, Q5, Q6, Q7, Q8, Q9, Q10, Q11]), "targets" : qUnion([Q12])});
        }
        {
            var Q0;
            Q0=makeQuery(id+"F1.opExtrude","SWEPT_FACE",FACE,{"disambiguationData":[OSD([sQuery(id+"F0.wireOp",EDGE,"E1.bottom")])]});
            var sketch = newSketch(context, id + "F15", { "sketchPlane" : qUnion([Q0])});
            skLineSegment(sketch, "E121", {"start": v(-26.45, -13.07) * mm, "end": v(-8.63, -13.07) * mm});
            skLineSegment(sketch, "E122", {"start": v(-26.45, -13.07) * mm, "end": v(-26.45, -53.88) * mm});
            skLineSegment(sketch, "E123", {"start": v(-26.45, -53.88) * mm, "end": v(-8.63, -13.07) * mm});
            skLineSegment(sketch, "E124", {"start": v(-21.64, -53.88) * mm, "end": v(-2.69, -53.88) * mm});
            skLineSegment(sketch, "E125", {"start": v(-2.69, -53.88) * mm, "end": v(-2.69, -13.28) * mm});
            skLineSegment(sketch, "E126", {"start": v(-2.69, -13.28) * mm, "end": v(-21.64, -53.88) * mm});
            skLineSegment(sketch, "E127.MirrorCS", {"start": v(26.53, -53.46) * mm, "end": v(11.1, -12.4) * mm});
            skLineSegment(sketch, "E128.MirrorCS", {"start": v(22.26, -53.46) * mm, "end": v(2.78, -53.46) * mm});
            skLineSegment(sketch, "E129.MirrorCS", {"start": v(2.78, -53.46) * mm, "end": v(3.48, -13.07) * mm});
            skLineSegment(sketch, "E130.MirrorCS", {"start": v(3.48, -13.07) * mm, "end": v(22.26, -53.46) * mm});
            skLineSegment(sketch, "E131.MirrorCS", {"start": v(27.25, -12.4) * mm, "end": v(26.53, -53.46) * mm});
            skLineSegment(sketch, "E132.MirrorCS", {"start": v(27.25, -12.4) * mm, "end": v(11.1, -12.4) * mm});
            skLineSegment(sketch, "E133.MirrorCS", {"start": v(22.26, -64.39) * mm, "end": v(2.78, -64.39) * mm});
            skLineSegment(sketch, "E134.MirrorCS", {"start": v(-2.69, -113.1) * mm, "end": v(-22.17, -64.39) * mm});
            skLineSegment(sketch, "E135.MirrorCS", {"start": v(2.78, -64.39) * mm, "end": v(2.78, -113.1) * mm});
            skLineSegment(sketch, "E136.MirrorCS", {"start": v(2.78, -113.1) * mm, "end": v(22.26, -64.39) * mm});
            skLineSegment(sketch, "E137.MirrorCS", {"start": v(-2.69, -64.39) * mm, "end": v(-2.69, -113.1) * mm});
            skLineSegment(sketch, "E138.MirrorCS", {"start": v(26.53, -64.39) * mm, "end": v(8.48, -113.1) * mm});
            skLineSegment(sketch, "E139.MirrorCS", {"start": v(-26.45, -64.39) * mm, "end": v(-8.4, -113.1) * mm});
            skLineSegment(sketch, "E140.MirrorCS", {"start": v(-26.45, -113.1) * mm, "end": v(-26.45, -64.39) * mm});
            skLineSegment(sketch, "E141.MirrorCS", {"start": v(-26.45, -113.1) * mm, "end": v(-8.4, -113.1) * mm});
            skLineSegment(sketch, "E142.MirrorCS", {"start": v(26.53, -113.1) * mm, "end": v(8.48, -113.1) * mm});
            skLineSegment(sketch, "E143.MirrorCS", {"start": v(-22.17, -64.39) * mm, "end": v(-2.69, -64.39) * mm});
            skLineSegment(sketch, "E144.MirrorCS", {"start": v(26.53, -113.1) * mm, "end": v(26.53, -64.39) * mm});
            skLineSegment(sketch, "E145.MirrorCS", {"start": v(26.53, -121.17) * mm, "end": v(26.53, -169.87) * mm});
            skLineSegment(sketch, "E146.MirrorCS", {"start": v(26.53, -169.87) * mm, "end": v(8.48, -121.17) * mm});
            skLineSegment(sketch, "E147.MirrorCS", {"start": v(26.53, -121.17) * mm, "end": v(8.48, -121.17) * mm});
            skLineSegment(sketch, "E148.MirrorCS", {"start": v(2.78, -121.17) * mm, "end": v(22.26, -169.87) * mm});
            skLineSegment(sketch, "E149.MirrorCS", {"start": v(-2.69, -121.17) * mm, "end": v(-22.17, -169.87) * mm});
            skLineSegment(sketch, "E150.MirrorCS", {"start": v(-26.45, -121.17) * mm, "end": v(-26.45, -169.87) * mm});
            skLineSegment(sketch, "E151.MirrorCS", {"start": v(-2.69, -169.87) * mm, "end": v(-2.69, -121.17) * mm});
            skLineSegment(sketch, "E152.MirrorCS", {"start": v(-26.45, -169.87) * mm, "end": v(-8.4, -121.17) * mm});
            skLineSegment(sketch, "E153.MirrorCS", {"start": v(-22.17, -169.87) * mm, "end": v(-2.69, -169.87) * mm});
            skLineSegment(sketch, "E154.MirrorCS", {"start": v(-26.45, -121.17) * mm, "end": v(-8.4, -121.17) * mm});
            skLineSegment(sketch, "E155.MirrorCS", {"start": v(22.26, -169.87) * mm, "end": v(2.78, -169.87) * mm});
            skLineSegment(sketch, "E156.MirrorCS", {"start": v(2.78, -169.87) * mm, "end": v(2.78, -121.17) * mm});
            skSolve(sketch);
        }
        {
            var Q0;
            Q0=makeQuery(id+"F15.imprint","IMPRINT",FACE,{"disambiguationData":[TD([[makeQuery(id+"F15.imprint","IMPRINT",EDGE,{"derivedFrom":sQuery(id+"F15.wireOp",EDGE,"E121")}),-1.0]])]});
            var Q1;
            Q1=makeQuery(id+"F15.imprint","IMPRINT",FACE,{"disambiguationData":[TD([[makeQuery(id+"F15.imprint","IMPRINT",EDGE,{"derivedFrom":sQuery(id+"F15.wireOp",EDGE,"E124")}),1.0]])]});
            var Q2;
            Q2=makeQuery(id+"F15.imprint","IMPRINT",FACE,{"disambiguationData":[TD([[makeQuery(id+"F15.imprint","IMPRINT",EDGE,{"derivedFrom":sQuery(id+"F15.wireOp",EDGE,"E128.MirrorCS")}),-1.0]])]});
            var Q3;
            Q3=makeQuery(id+"F15.imprint","IMPRINT",FACE,{"disambiguationData":[TD([[makeQuery(id+"F15.imprint","IMPRINT",EDGE,{"derivedFrom":sQuery(id+"F15.wireOp",EDGE,"E127.MirrorCS")}),-1.0]])]});
            var Q4;
            Q4=makeQuery(id+"F15.imprint","IMPRINT",FACE,{"disambiguationData":[TD([[makeQuery(id+"F15.imprint","IMPRINT",EDGE,{"derivedFrom":sQuery(id+"F15.wireOp",EDGE,"E139.MirrorCS")}),-1.0]])]});
            var Q5;
            Q5=makeQuery(id+"F15.imprint","IMPRINT",FACE,{"disambiguationData":[TD([[makeQuery(id+"F15.imprint","IMPRINT",EDGE,{"derivedFrom":sQuery(id+"F15.wireOp",EDGE,"E134.MirrorCS")}),-1.0]])]});
            var Q6;
            Q6=makeQuery(id+"F15.imprint","IMPRINT",FACE,{"disambiguationData":[TD([[makeQuery(id+"F15.imprint","IMPRINT",EDGE,{"derivedFrom":sQuery(id+"F15.wireOp",EDGE,"E133.MirrorCS")}),1.0]])]});
            var Q7;
            Q7=makeQuery(id+"F15.imprint","IMPRINT",FACE,{"disambiguationData":[TD([[makeQuery(id+"F15.imprint","IMPRINT",EDGE,{"derivedFrom":sQuery(id+"F15.wireOp",EDGE,"E138.MirrorCS")}),1.0]])]});
            var Q8;
            Q8=makeQuery(id+"F15.imprint","IMPRINT",FACE,{"disambiguationData":[TD([[makeQuery(id+"F15.imprint","IMPRINT",EDGE,{"derivedFrom":sQuery(id+"F15.wireOp",EDGE,"E145.MirrorCS")}),-1.0]])]});
            var Q9;
            Q9=makeQuery(id+"F15.imprint","IMPRINT",FACE,{"disambiguationData":[TD([[makeQuery(id+"F15.imprint","IMPRINT",EDGE,{"derivedFrom":sQuery(id+"F15.wireOp",EDGE,"E148.MirrorCS")}),-1.0]])]});
            var Q10;
            Q10=makeQuery(id+"F15.imprint","IMPRINT",FACE,{"disambiguationData":[TD([[makeQuery(id+"F15.imprint","IMPRINT",EDGE,{"derivedFrom":sQuery(id+"F15.wireOp",EDGE,"E149.MirrorCS")}),1.0]])]});
            var Q11;
            Q11=makeQuery(id+"F15.imprint","IMPRINT",FACE,{"disambiguationData":[TD([[makeQuery(id+"F15.imprint","IMPRINT",EDGE,{"derivedFrom":sQuery(id+"F15.wireOp",EDGE,"E150.MirrorCS")}),1.0]])]});
            extrude(context, id + "F16", {"entities" : qUnion([Q0, Q1, Q2, Q3, Q4, Q5, Q6, Q7, Q8, Q9, Q10, Q11]), "oppositeDirection" : true, "depth" : 5 * mm, "offsetDistance" : 25 * mm});
        }
        {
            var Q0;
            Q0=makeQuery(id+"F16.opExtrude","SWEPT_BODY",BODY,{"disambiguationData":[OSD([sQuery(id+"F15.wireOp",EDGE,"E127.MirrorCS"),sQuery(id+"F15.wireOp",EDGE,"E131.MirrorCS"),sQuery(id+"F15.wireOp",EDGE,"E132.MirrorCS")])]});
            var Q1;
            Q1=makeQuery(id+"F16.opExtrude","SWEPT_BODY",BODY,{"disambiguationData":[OSD([sQuery(id+"F15.wireOp",EDGE,"E121"),sQuery(id+"F15.wireOp",EDGE,"E122"),sQuery(id+"F15.wireOp",EDGE,"E123")])]});
            var Q2;
            Q2=makeQuery(id+"F16.opExtrude","SWEPT_BODY",BODY,{"disambiguationData":[OSD([sQuery(id+"F15.wireOp",EDGE,"E124"),sQuery(id+"F15.wireOp",EDGE,"E125"),sQuery(id+"F15.wireOp",EDGE,"E126")])]});
            var Q3;
            Q3=makeQuery(id+"F16.opExtrude","SWEPT_BODY",BODY,{"disambiguationData":[OSD([sQuery(id+"F15.wireOp",EDGE,"E128.MirrorCS"),sQuery(id+"F15.wireOp",EDGE,"E129.MirrorCS"),sQuery(id+"F15.wireOp",EDGE,"E130.MirrorCS")])]});
            var Q4;
            Q4=makeQuery(id+"F16.opExtrude","SWEPT_BODY",BODY,{"disambiguationData":[OSD([sQuery(id+"F15.wireOp",EDGE,"E139.MirrorCS"),sQuery(id+"F15.wireOp",EDGE,"E140.MirrorCS"),sQuery(id+"F15.wireOp",EDGE,"E141.MirrorCS")])]});
            var Q5;
            Q5=makeQuery(id+"F16.opExtrude","SWEPT_BODY",BODY,{"disambiguationData":[OSD([sQuery(id+"F15.wireOp",EDGE,"E134.MirrorCS"),sQuery(id+"F15.wireOp",EDGE,"E137.MirrorCS"),sQuery(id+"F15.wireOp",EDGE,"E143.MirrorCS")])]});
            var Q6;
            Q6=makeQuery(id+"F16.opExtrude","SWEPT_BODY",BODY,{"disambiguationData":[OSD([sQuery(id+"F15.wireOp",EDGE,"E133.MirrorCS"),sQuery(id+"F15.wireOp",EDGE,"E135.MirrorCS"),sQuery(id+"F15.wireOp",EDGE,"E136.MirrorCS")])]});
            var Q7;
            Q7=makeQuery(id+"F16.opExtrude","SWEPT_BODY",BODY,{"disambiguationData":[OSD([sQuery(id+"F15.wireOp",EDGE,"E138.MirrorCS"),sQuery(id+"F15.wireOp",EDGE,"E142.MirrorCS"),sQuery(id+"F15.wireOp",EDGE,"E144.MirrorCS")])]});
            var Q8;
            Q8=makeQuery(id+"F16.opExtrude","SWEPT_BODY",BODY,{"disambiguationData":[OSD([sQuery(id+"F15.wireOp",EDGE,"E150.MirrorCS"),sQuery(id+"F15.wireOp",EDGE,"E152.MirrorCS"),sQuery(id+"F15.wireOp",EDGE,"E154.MirrorCS")])]});
            var Q9;
            Q9=makeQuery(id+"F16.opExtrude","SWEPT_BODY",BODY,{"disambiguationData":[OSD([sQuery(id+"F15.wireOp",EDGE,"E149.MirrorCS"),sQuery(id+"F15.wireOp",EDGE,"E151.MirrorCS"),sQuery(id+"F15.wireOp",EDGE,"E153.MirrorCS")])]});
            var Q10;
            Q10=makeQuery(id+"F16.opExtrude","SWEPT_BODY",BODY,{"disambiguationData":[OSD([sQuery(id+"F15.wireOp",EDGE,"E148.MirrorCS"),sQuery(id+"F15.wireOp",EDGE,"E155.MirrorCS"),sQuery(id+"F15.wireOp",EDGE,"E156.MirrorCS")])]});
            var Q11;
            Q11=makeQuery(id+"F16.opExtrude","SWEPT_BODY",BODY,{"disambiguationData":[OSD([sQuery(id+"F15.wireOp",EDGE,"E145.MirrorCS"),sQuery(id+"F15.wireOp",EDGE,"E146.MirrorCS"),sQuery(id+"F15.wireOp",EDGE,"E147.MirrorCS")])]});
            var Q12;
            Q12=makeQuery(id+"F1.opExtrude","SWEPT_BODY",BODY,{"disambiguationData":[OSD([sQuery(id+"F0.wireOp",EDGE,"E0.bottom"),sQuery(id+"F0.wireOp",EDGE,"E0.top"),sQuery(id+"F0.wireOp",EDGE,"E0.left"),sQuery(id+"F0.wireOp",EDGE,"E0.right"),sQuery(id+"F0.wireOp",EDGE,"E1.bottom"),sQuery(id+"F0.wireOp",EDGE,"E1.top"),sQuery(id+"F0.wireOp",EDGE,"E1.left"),sQuery(id+"F0.wireOp",EDGE,"E1.right")])]});
            booleanBodies(context, id + "F17", {"operationType" : BooleanOperationType.SUBTRACTION, "tools" : qUnion([Q0, Q1, Q2, Q3, Q4, Q5, Q6, Q7, Q8, Q9, Q10, Q11]), "targets" : qUnion([Q12])});
        }
    });
